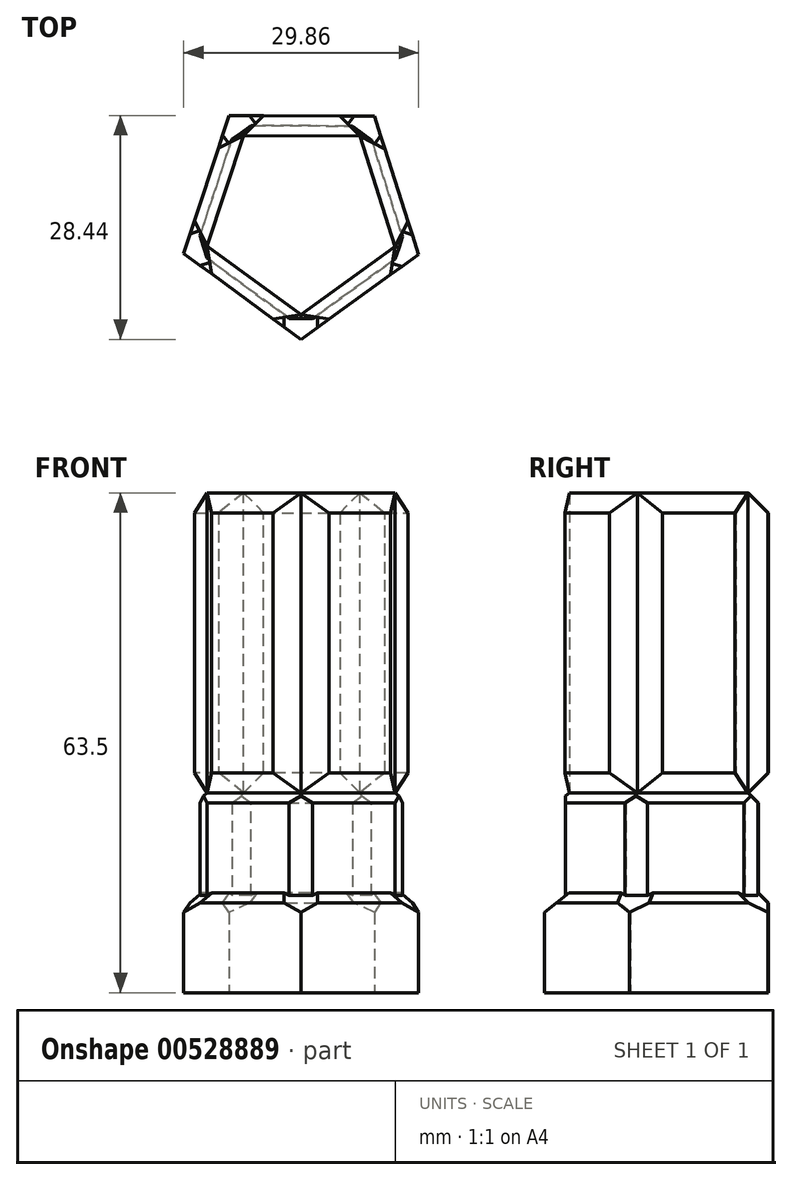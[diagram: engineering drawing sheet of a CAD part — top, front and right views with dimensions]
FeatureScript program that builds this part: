
annotation { "Feature Type Name" : "Feature", "Feature Type Description" : "" }
export const myFeature = defineFeature(function(context is Context, id is Id, definition is map)
    precondition{}
    {
        {
            var Q0;
            Q0=qCreatedBy(makeId("Top.planeOp"),FACE);
            var sketch = newSketch(context, id + "F0", { "sketchPlane" : qUnion([Q0])});
            skCircle(sketch, "E0.cCircle", {"center": v(-32.15, -43.23) * mm, "radius": 12.7 * mm, "construction": true});
            skLineSegment(sketch, "E0.0", {"start": v(-17.24, -48.15) * mm, "end": v(-32.22, -58.93) * mm});
            skLineSegment(sketch, "E0.1", {"start": v(-32.22, -58.93) * mm, "end": v(-47.1, -48.01) * mm});
            skLineSegment(sketch, "E0.2", {"start": v(-47.1, -48.01) * mm, "end": v(-41.32, -30.49) * mm});
            skLineSegment(sketch, "E0.3", {"start": v(-41.32, -30.49) * mm, "end": v(-22.86, -30.58) * mm});
            skLineSegment(sketch, "E0.4", {"start": v(-22.86, -30.58) * mm, "end": v(-17.24, -48.15) * mm});
            skPoint(sketch, "E0.0.midPoint", {"position": v(-24.73, -53.54) * mm});
            skSolve(sketch);
        }
        {
            var Q0;
            Q0=makeQuery(id+"F0.imprint","IMPRINT",FACE,{"disambiguationData":[TD([[makeQuery(id+"F0.imprint","IMPRINT",EDGE,{"derivedFrom":sQuery(id+"F0.wireOp",EDGE,"E0.0")}),-1.0]])]});
            extrude(context, id + "F1", {"entities" : qUnion([Q0]), "depth" : 12.7 * mm, "offsetDistance" : 25.4 * mm});
        }
        {
            var Q0;
            Q0=makeQuery(id+"F1.opExtrude","CAP_FACE",FACE,{"disambiguationData":[OSD([sQuery(id+"F0.wireOp",EDGE,"E0.0"),sQuery(id+"F0.wireOp",EDGE,"E0.1"),sQuery(id+"F0.wireOp",EDGE,"E0.2"),sQuery(id+"F0.wireOp",EDGE,"E0.3"),sQuery(id+"F0.wireOp",EDGE,"E0.4")])],"isStart":false});
            chamfer(context, id + "F2", {"entities" : qUnion([Q0]), "width" : 1.27 * mm, "tangentPropagation" : true});
        }
        {
            var Q0;
            Q0=makeQuery(id+"F1.opExtrude","CAP_FACE",FACE,{"disambiguationData":[OSD([sQuery(id+"F0.wireOp",EDGE,"E0.0"),sQuery(id+"F0.wireOp",EDGE,"E0.1"),sQuery(id+"F0.wireOp",EDGE,"E0.2"),sQuery(id+"F0.wireOp",EDGE,"E0.3"),sQuery(id+"F0.wireOp",EDGE,"E0.4")])],"isStart":false});
            extrude(context, id + "F3", {"entities" : qUnion([Q0]), "operationType" : NewBodyOperationType.ADD, "depth" : 12.7 * mm, "offsetDistance" : 25.4 * mm});
        }
        {
            var Q0;
            Q0=makeQuery(id+"F3.opExtrude","CAP_FACE",FACE,{"disambiguationData":[OSD([sQuery(id+"F0.wireOp",EDGE,"E0.0"),sQuery(id+"F0.wireOp",EDGE,"E0.1"),sQuery(id+"F0.wireOp",EDGE,"E0.2"),sQuery(id+"F0.wireOp",EDGE,"E0.3"),sQuery(id+"F0.wireOp",EDGE,"E0.4")])],"isStart":false});
            chamfer(context, id + "F4", {"entities" : qUnion([Q0]), "width" : 1.27 * mm, "tangentPropagation" : true});
        }
        {
            var Q0;
            Q0=makeQuery(id+"F3.opExtrude","CAP_FACE",FACE,{"disambiguationData":[OSD([sQuery(id+"F0.wireOp",EDGE,"E0.0"),sQuery(id+"F0.wireOp",EDGE,"E0.1"),sQuery(id+"F0.wireOp",EDGE,"E0.2"),sQuery(id+"F0.wireOp",EDGE,"E0.3"),sQuery(id+"F0.wireOp",EDGE,"E0.4")])],"isStart":false});
            extrude(context, id + "F5", {"entities" : qUnion([Q0]), "operationType" : NewBodyOperationType.ADD, "depth" : 38.1 * mm, "offsetDistance" : 25.4 * mm});
        }
        {
            var Q0;
            {var subQ0=sQuery(id+"F0.wireOp",EDGE,"E0.4");var subQ1=sQuery(id+"F0.wireOp",EDGE,"E0.3");var subQ2=sQuery(id+"F0.wireOp",EDGE,"E0.2");var subQ3=sQuery(id+"F0.wireOp",EDGE,"E0.1");var subQ4=sQuery(id+"F0.wireOp",EDGE,"E0.0");Q0=makeQuery(id+"F3.opExtrude","SWEPT_EDGE",EDGE,{"disambiguationData":[OSD([subQ4,subQ3,subQ2,subQ1,subQ0]),TDD([makeQuery(id+"F2.opChamfer","BLEND_VERTEX",VERTEX,{"blendedFrom":[makeQuery(id+"F1.opExtrude","CAP_EDGE",EDGE,{"disambiguationData":[OSD([subQ4])],"isStart":false}),makeQuery(id+"F1.opExtrude","CAP_EDGE",EDGE,{"disambiguationData":[OSD([subQ0])],"isStart":false}),makeQuery(id+"F1.opExtrude","CAP_FACE",FACE,{"disambiguationData":[OSD([subQ4,subQ3,subQ2,subQ1,subQ0])],"isStart":false})],"blendedInto":[makeQuery(id+"F1.opExtrude","CAP_FACE",FACE,{"disambiguationData":[OSD([subQ4,subQ3,subQ2,subQ1,subQ0])],"isStart":false})]})])]});}
            var Q1;
            {var subQ0=sQuery(id+"F0.wireOp",EDGE,"E0.4");var subQ1=sQuery(id+"F0.wireOp",EDGE,"E0.3");var subQ2=sQuery(id+"F0.wireOp",EDGE,"E0.2");var subQ3=sQuery(id+"F0.wireOp",EDGE,"E0.1");var subQ4=sQuery(id+"F0.wireOp",EDGE,"E0.0");Q1=makeQuery(id+"F3.opExtrude","SWEPT_EDGE",EDGE,{"disambiguationData":[OSD([subQ4,subQ3,subQ2,subQ1,subQ0]),TDD([makeQuery(id+"F2.opChamfer","BLEND_VERTEX",VERTEX,{"blendedFrom":[makeQuery(id+"F1.opExtrude","CAP_EDGE",EDGE,{"disambiguationData":[OSD([subQ4])],"isStart":false}),makeQuery(id+"F1.opExtrude","CAP_EDGE",EDGE,{"disambiguationData":[OSD([subQ3])],"isStart":false}),makeQuery(id+"F1.opExtrude","CAP_FACE",FACE,{"disambiguationData":[OSD([subQ4,subQ3,subQ2,subQ1,subQ0])],"isStart":false})],"blendedInto":[makeQuery(id+"F1.opExtrude","CAP_FACE",FACE,{"disambiguationData":[OSD([subQ4,subQ3,subQ2,subQ1,subQ0])],"isStart":false})]})])]});}
            var Q2;
            {var subQ0=sQuery(id+"F0.wireOp",EDGE,"E0.4");var subQ1=sQuery(id+"F0.wireOp",EDGE,"E0.3");var subQ2=sQuery(id+"F0.wireOp",EDGE,"E0.2");var subQ3=sQuery(id+"F0.wireOp",EDGE,"E0.1");var subQ4=sQuery(id+"F0.wireOp",EDGE,"E0.0");Q2=makeQuery(id+"F3.opExtrude","SWEPT_EDGE",EDGE,{"disambiguationData":[OSD([subQ4,subQ3,subQ2,subQ1,subQ0]),TDD([makeQuery(id+"F2.opChamfer","BLEND_VERTEX",VERTEX,{"blendedFrom":[makeQuery(id+"F1.opExtrude","CAP_EDGE",EDGE,{"disambiguationData":[OSD([subQ3])],"isStart":false}),makeQuery(id+"F1.opExtrude","CAP_EDGE",EDGE,{"disambiguationData":[OSD([subQ2])],"isStart":false}),makeQuery(id+"F1.opExtrude","CAP_FACE",FACE,{"disambiguationData":[OSD([subQ4,subQ3,subQ2,subQ1,subQ0])],"isStart":false})],"blendedInto":[makeQuery(id+"F1.opExtrude","CAP_FACE",FACE,{"disambiguationData":[OSD([subQ4,subQ3,subQ2,subQ1,subQ0])],"isStart":false})]})])]});}
            var Q3;
            {var subQ0=sQuery(id+"F0.wireOp",EDGE,"E0.4");var subQ1=sQuery(id+"F0.wireOp",EDGE,"E0.3");var subQ2=sQuery(id+"F0.wireOp",EDGE,"E0.2");var subQ3=sQuery(id+"F0.wireOp",EDGE,"E0.1");var subQ4=sQuery(id+"F0.wireOp",EDGE,"E0.0");Q3=makeQuery(id+"F3.opExtrude","SWEPT_EDGE",EDGE,{"disambiguationData":[OSD([subQ4,subQ3,subQ2,subQ1,subQ0]),TDD([makeQuery(id+"F2.opChamfer","BLEND_VERTEX",VERTEX,{"blendedFrom":[makeQuery(id+"F1.opExtrude","CAP_EDGE",EDGE,{"disambiguationData":[OSD([subQ2])],"isStart":false}),makeQuery(id+"F1.opExtrude","CAP_EDGE",EDGE,{"disambiguationData":[OSD([subQ1])],"isStart":false}),makeQuery(id+"F1.opExtrude","CAP_FACE",FACE,{"disambiguationData":[OSD([subQ4,subQ3,subQ2,subQ1,subQ0])],"isStart":false})],"blendedInto":[makeQuery(id+"F1.opExtrude","CAP_FACE",FACE,{"disambiguationData":[OSD([subQ4,subQ3,subQ2,subQ1,subQ0])],"isStart":false})]})])]});}
            var Q4;
            {var subQ0=sQuery(id+"F0.wireOp",EDGE,"E0.4");var subQ1=sQuery(id+"F0.wireOp",EDGE,"E0.3");var subQ2=sQuery(id+"F0.wireOp",EDGE,"E0.2");var subQ3=sQuery(id+"F0.wireOp",EDGE,"E0.1");var subQ4=sQuery(id+"F0.wireOp",EDGE,"E0.0");Q4=makeQuery(id+"F3.opExtrude","SWEPT_EDGE",EDGE,{"disambiguationData":[OSD([subQ4,subQ3,subQ2,subQ1,subQ0]),TDD([makeQuery(id+"F2.opChamfer","BLEND_VERTEX",VERTEX,{"blendedFrom":[makeQuery(id+"F1.opExtrude","CAP_EDGE",EDGE,{"disambiguationData":[OSD([subQ1])],"isStart":false}),makeQuery(id+"F1.opExtrude","CAP_EDGE",EDGE,{"disambiguationData":[OSD([subQ0])],"isStart":false}),makeQuery(id+"F1.opExtrude","CAP_FACE",FACE,{"disambiguationData":[OSD([subQ4,subQ3,subQ2,subQ1,subQ0])],"isStart":false})],"blendedInto":[makeQuery(id+"F1.opExtrude","CAP_FACE",FACE,{"disambiguationData":[OSD([subQ4,subQ3,subQ2,subQ1,subQ0])],"isStart":false})]})])]});}
            chamfer(context, id + "F6", {"entities" : qUnion([Q0, Q1, Q2, Q3, Q4]), "width" : 2.54 * mm, "tangentPropagation" : true});
        }
        {
            var Q0;
            {var subQ0=sQuery(id+"F0.wireOp",EDGE,"E0.4");var subQ1=sQuery(id+"F0.wireOp",EDGE,"E0.3");var subQ2=sQuery(id+"F0.wireOp",EDGE,"E0.2");var subQ3=sQuery(id+"F0.wireOp",EDGE,"E0.1");var subQ4=sQuery(id+"F0.wireOp",EDGE,"E0.0");Q0=makeQuery(id+"F5.opExtrude","SWEPT_FACE",FACE,{"disambiguationData":[OSD([subQ4,subQ3,subQ2,subQ1,subQ0]),TDD([makeQuery(id+"F4.opChamfer","BLEND_EDGE",EDGE,{"blendedFrom":[makeQuery(id+"F3.opExtrude","CAP_EDGE",EDGE,{"disambiguationData":[OSD([subQ4,subQ3,subQ2,subQ1,subQ0]),TDD([makeQuery(id+"F2.opChamfer","BLEND_EDGE",EDGE,{"blendedFrom":[makeQuery(id+"F1.opExtrude","CAP_EDGE",EDGE,{"disambiguationData":[OSD([subQ1])],"isStart":false}),makeQuery(id+"F1.opExtrude","CAP_FACE",FACE,{"disambiguationData":[OSD([subQ4,subQ3,subQ2,subQ1,subQ0])],"isStart":false})],"blendedInto":[makeQuery(id+"F1.opExtrude","CAP_FACE",FACE,{"disambiguationData":[OSD([subQ4,subQ3,subQ2,subQ1,subQ0])],"isStart":false})]})])],"isStart":false}),makeQuery(id+"F3.opExtrude","CAP_FACE",FACE,{"disambiguationData":[OSD([subQ4,subQ3,subQ2,subQ1,subQ0])],"isStart":false})],"blendedInto":[makeQuery(id+"F3.opExtrude","CAP_FACE",FACE,{"disambiguationData":[OSD([subQ4,subQ3,subQ2,subQ1,subQ0])],"isStart":false})]})])]});}
            extrude(context, id + "F7", {"entities" : qUnion([Q0]), "operationType" : NewBodyOperationType.ADD, "depth" : 2.54 * mm, "offsetDistance" : 25.4 * mm});
        }
        {
            var Q0;
            {var subQ0=sQuery(id+"F0.wireOp",EDGE,"E0.4");var subQ1=sQuery(id+"F0.wireOp",EDGE,"E0.3");var subQ2=sQuery(id+"F0.wireOp",EDGE,"E0.2");var subQ3=sQuery(id+"F0.wireOp",EDGE,"E0.1");var subQ4=sQuery(id+"F0.wireOp",EDGE,"E0.0");Q0=makeQuery(id+"F5.opExtrude","SWEPT_FACE",FACE,{"disambiguationData":[OSD([subQ4,subQ3,subQ2,subQ1,subQ0]),TDD([makeQuery(id+"F4.opChamfer","BLEND_EDGE",EDGE,{"blendedFrom":[makeQuery(id+"F3.opExtrude","CAP_EDGE",EDGE,{"disambiguationData":[OSD([subQ4,subQ3,subQ2,subQ1,subQ0]),TDD([makeQuery(id+"F2.opChamfer","BLEND_EDGE",EDGE,{"blendedFrom":[makeQuery(id+"F1.opExtrude","CAP_EDGE",EDGE,{"disambiguationData":[OSD([subQ2])],"isStart":false}),makeQuery(id+"F1.opExtrude","CAP_FACE",FACE,{"disambiguationData":[OSD([subQ4,subQ3,subQ2,subQ1,subQ0])],"isStart":false})],"blendedInto":[makeQuery(id+"F1.opExtrude","CAP_FACE",FACE,{"disambiguationData":[OSD([subQ4,subQ3,subQ2,subQ1,subQ0])],"isStart":false})]})])],"isStart":false}),makeQuery(id+"F3.opExtrude","CAP_FACE",FACE,{"disambiguationData":[OSD([subQ4,subQ3,subQ2,subQ1,subQ0])],"isStart":false})],"blendedInto":[makeQuery(id+"F3.opExtrude","CAP_FACE",FACE,{"disambiguationData":[OSD([subQ4,subQ3,subQ2,subQ1,subQ0])],"isStart":false})]})])]});}
            extrude(context, id + "F8", {"entities" : qUnion([Q0]), "operationType" : NewBodyOperationType.ADD, "depth" : 2.54 * mm, "offsetDistance" : 25.4 * mm});
        }
        {
            var Q0;
            {var subQ0=sQuery(id+"F0.wireOp",EDGE,"E0.4");var subQ1=sQuery(id+"F0.wireOp",EDGE,"E0.3");var subQ2=sQuery(id+"F0.wireOp",EDGE,"E0.2");var subQ3=sQuery(id+"F0.wireOp",EDGE,"E0.1");var subQ4=sQuery(id+"F0.wireOp",EDGE,"E0.0");Q0=makeQuery(id+"F5.opExtrude","SWEPT_FACE",FACE,{"disambiguationData":[OSD([subQ4,subQ3,subQ2,subQ1,subQ0]),TDD([makeQuery(id+"F4.opChamfer","BLEND_EDGE",EDGE,{"blendedFrom":[makeQuery(id+"F3.opExtrude","CAP_EDGE",EDGE,{"disambiguationData":[OSD([subQ4,subQ3,subQ2,subQ1,subQ0]),TDD([makeQuery(id+"F2.opChamfer","BLEND_EDGE",EDGE,{"blendedFrom":[makeQuery(id+"F1.opExtrude","CAP_EDGE",EDGE,{"disambiguationData":[OSD([subQ3])],"isStart":false}),makeQuery(id+"F1.opExtrude","CAP_FACE",FACE,{"disambiguationData":[OSD([subQ4,subQ3,subQ2,subQ1,subQ0])],"isStart":false})],"blendedInto":[makeQuery(id+"F1.opExtrude","CAP_FACE",FACE,{"disambiguationData":[OSD([subQ4,subQ3,subQ2,subQ1,subQ0])],"isStart":false})]})])],"isStart":false}),makeQuery(id+"F3.opExtrude","CAP_FACE",FACE,{"disambiguationData":[OSD([subQ4,subQ3,subQ2,subQ1,subQ0])],"isStart":false})],"blendedInto":[makeQuery(id+"F3.opExtrude","CAP_FACE",FACE,{"disambiguationData":[OSD([subQ4,subQ3,subQ2,subQ1,subQ0])],"isStart":false})]})])]});}
            extrude(context, id + "F9", {"entities" : qUnion([Q0]), "operationType" : NewBodyOperationType.ADD, "depth" : 2.54 * mm, "offsetDistance" : 25.4 * mm});
        }
        {
            var Q0;
            {var subQ0=sQuery(id+"F0.wireOp",EDGE,"E0.4");var subQ1=sQuery(id+"F0.wireOp",EDGE,"E0.3");var subQ2=sQuery(id+"F0.wireOp",EDGE,"E0.2");var subQ3=sQuery(id+"F0.wireOp",EDGE,"E0.1");var subQ4=sQuery(id+"F0.wireOp",EDGE,"E0.0");Q0=makeQuery(id+"F5.opExtrude","SWEPT_FACE",FACE,{"disambiguationData":[OSD([subQ4,subQ3,subQ2,subQ1,subQ0]),TDD([makeQuery(id+"F4.opChamfer","BLEND_EDGE",EDGE,{"blendedFrom":[makeQuery(id+"F3.opExtrude","CAP_EDGE",EDGE,{"disambiguationData":[OSD([subQ4,subQ3,subQ2,subQ1,subQ0]),TDD([makeQuery(id+"F2.opChamfer","BLEND_EDGE",EDGE,{"blendedFrom":[makeQuery(id+"F1.opExtrude","CAP_EDGE",EDGE,{"disambiguationData":[OSD([subQ4])],"isStart":false}),makeQuery(id+"F1.opExtrude","CAP_FACE",FACE,{"disambiguationData":[OSD([subQ4,subQ3,subQ2,subQ1,subQ0])],"isStart":false})],"blendedInto":[makeQuery(id+"F1.opExtrude","CAP_FACE",FACE,{"disambiguationData":[OSD([subQ4,subQ3,subQ2,subQ1,subQ0])],"isStart":false})]})])],"isStart":false}),makeQuery(id+"F3.opExtrude","CAP_FACE",FACE,{"disambiguationData":[OSD([subQ4,subQ3,subQ2,subQ1,subQ0])],"isStart":false})],"blendedInto":[makeQuery(id+"F3.opExtrude","CAP_FACE",FACE,{"disambiguationData":[OSD([subQ4,subQ3,subQ2,subQ1,subQ0])],"isStart":false})]})])]});}
            extrude(context, id + "F10", {"entities" : qUnion([Q0]), "operationType" : NewBodyOperationType.ADD, "depth" : 2.54 * mm, "offsetDistance" : 25.4 * mm});
        }
        {
            var Q0;
            {var subQ0=sQuery(id+"F0.wireOp",EDGE,"E0.4");var subQ1=sQuery(id+"F0.wireOp",EDGE,"E0.3");var subQ2=sQuery(id+"F0.wireOp",EDGE,"E0.2");var subQ3=sQuery(id+"F0.wireOp",EDGE,"E0.1");var subQ4=sQuery(id+"F0.wireOp",EDGE,"E0.0");Q0=makeQuery(id+"F5.opExtrude","SWEPT_FACE",FACE,{"disambiguationData":[OSD([subQ4,subQ3,subQ2,subQ1,subQ0]),TDD([makeQuery(id+"F4.opChamfer","BLEND_EDGE",EDGE,{"blendedFrom":[makeQuery(id+"F3.opExtrude","CAP_EDGE",EDGE,{"disambiguationData":[OSD([subQ4,subQ3,subQ2,subQ1,subQ0]),TDD([makeQuery(id+"F2.opChamfer","BLEND_EDGE",EDGE,{"blendedFrom":[makeQuery(id+"F1.opExtrude","CAP_EDGE",EDGE,{"disambiguationData":[OSD([subQ0])],"isStart":false}),makeQuery(id+"F1.opExtrude","CAP_FACE",FACE,{"disambiguationData":[OSD([subQ4,subQ3,subQ2,subQ1,subQ0])],"isStart":false})],"blendedInto":[makeQuery(id+"F1.opExtrude","CAP_FACE",FACE,{"disambiguationData":[OSD([subQ4,subQ3,subQ2,subQ1,subQ0])],"isStart":false})]})])],"isStart":false}),makeQuery(id+"F3.opExtrude","CAP_FACE",FACE,{"disambiguationData":[OSD([subQ4,subQ3,subQ2,subQ1,subQ0])],"isStart":false})],"blendedInto":[makeQuery(id+"F3.opExtrude","CAP_FACE",FACE,{"disambiguationData":[OSD([subQ4,subQ3,subQ2,subQ1,subQ0])],"isStart":false})]})])]});}
            extrude(context, id + "F11", {"entities" : qUnion([Q0]), "operationType" : NewBodyOperationType.ADD, "depth" : 2.54 * mm, "offsetDistance" : 25.4 * mm});
        }
        {
            var Q0;
            Q0=makeQuery(id+"F10.opExtrude","CAP_FACE",FACE,{"disambiguationData":[OSD([sQuery(id+"F0.wireOp",EDGE,"E0.0"),sQuery(id+"F0.wireOp",EDGE,"E0.1"),sQuery(id+"F0.wireOp",EDGE,"E0.2"),sQuery(id+"F0.wireOp",EDGE,"E0.3"),sQuery(id+"F0.wireOp",EDGE,"E0.4")])],"isStart":false});
            chamfer(context, id + "F12", {"entities" : qUnion([Q0]), "width" : 2.54 * mm, "tangentPropagation" : true});
        }
        {
            var Q0;
            Q0=makeQuery(id+"F11.opExtrude","CAP_FACE",FACE,{"disambiguationData":[OSD([sQuery(id+"F0.wireOp",EDGE,"E0.0"),sQuery(id+"F0.wireOp",EDGE,"E0.1"),sQuery(id+"F0.wireOp",EDGE,"E0.2"),sQuery(id+"F0.wireOp",EDGE,"E0.3"),sQuery(id+"F0.wireOp",EDGE,"E0.4")])],"isStart":false});
            var Q1;
            Q1=makeQuery(id+"F7.opExtrude","CAP_FACE",FACE,{"disambiguationData":[OSD([sQuery(id+"F0.wireOp",EDGE,"E0.0"),sQuery(id+"F0.wireOp",EDGE,"E0.1"),sQuery(id+"F0.wireOp",EDGE,"E0.2"),sQuery(id+"F0.wireOp",EDGE,"E0.3"),sQuery(id+"F0.wireOp",EDGE,"E0.4")])],"isStart":false});
            var Q2;
            Q2=makeQuery(id+"F8.opExtrude","CAP_FACE",FACE,{"disambiguationData":[OSD([sQuery(id+"F0.wireOp",EDGE,"E0.0"),sQuery(id+"F0.wireOp",EDGE,"E0.1"),sQuery(id+"F0.wireOp",EDGE,"E0.2"),sQuery(id+"F0.wireOp",EDGE,"E0.3"),sQuery(id+"F0.wireOp",EDGE,"E0.4")])],"isStart":false});
            var Q3;
            Q3=makeQuery(id+"F9.opExtrude","CAP_FACE",FACE,{"disambiguationData":[OSD([sQuery(id+"F0.wireOp",EDGE,"E0.0"),sQuery(id+"F0.wireOp",EDGE,"E0.1"),sQuery(id+"F0.wireOp",EDGE,"E0.2"),sQuery(id+"F0.wireOp",EDGE,"E0.3"),sQuery(id+"F0.wireOp",EDGE,"E0.4")])],"isStart":false});
            chamfer(context, id + "F13", {"entities" : qUnion([Q0, Q1, Q2, Q3]), "width" : 2.54 * mm, "tangentPropagation" : true});
        }
        {
            var Q0;
            Q0=makeQuery(id+"F2.opChamfer","BLEND_EDGE",EDGE,{"blendedFrom":[makeQuery(id+"F1.opExtrude","CAP_EDGE",EDGE,{"disambiguationData":[OSD([sQuery(id+"F0.wireOp",EDGE,"E0.0")])],"isStart":false}),makeQuery(id+"F1.opExtrude","CAP_EDGE",EDGE,{"disambiguationData":[OSD([sQuery(id+"F0.wireOp",EDGE,"E0.1")])],"isStart":false})],"blendedInto":[]});
            var Q1;
            Q1=makeQuery(id+"F2.opChamfer","BLEND_EDGE",EDGE,{"blendedFrom":[makeQuery(id+"F1.opExtrude","CAP_EDGE",EDGE,{"disambiguationData":[OSD([sQuery(id+"F0.wireOp",EDGE,"E0.0")])],"isStart":false}),makeQuery(id+"F1.opExtrude","CAP_EDGE",EDGE,{"disambiguationData":[OSD([sQuery(id+"F0.wireOp",EDGE,"E0.4")])],"isStart":false})],"blendedInto":[]});
            var Q2;
            Q2=makeQuery(id+"F2.opChamfer","BLEND_EDGE",EDGE,{"blendedFrom":[makeQuery(id+"F1.opExtrude","CAP_EDGE",EDGE,{"disambiguationData":[OSD([sQuery(id+"F0.wireOp",EDGE,"E0.3")])],"isStart":false}),makeQuery(id+"F1.opExtrude","CAP_EDGE",EDGE,{"disambiguationData":[OSD([sQuery(id+"F0.wireOp",EDGE,"E0.4")])],"isStart":false})],"blendedInto":[]});
            var Q3;
            Q3=makeQuery(id+"F2.opChamfer","BLEND_EDGE",EDGE,{"blendedFrom":[makeQuery(id+"F1.opExtrude","CAP_EDGE",EDGE,{"disambiguationData":[OSD([sQuery(id+"F0.wireOp",EDGE,"E0.2")])],"isStart":false}),makeQuery(id+"F1.opExtrude","CAP_EDGE",EDGE,{"disambiguationData":[OSD([sQuery(id+"F0.wireOp",EDGE,"E0.3")])],"isStart":false})],"blendedInto":[]});
            var Q4;
            Q4=makeQuery(id+"F2.opChamfer","BLEND_EDGE",EDGE,{"blendedFrom":[makeQuery(id+"F1.opExtrude","CAP_EDGE",EDGE,{"disambiguationData":[OSD([sQuery(id+"F0.wireOp",EDGE,"E0.1")])],"isStart":false}),makeQuery(id+"F1.opExtrude","CAP_EDGE",EDGE,{"disambiguationData":[OSD([sQuery(id+"F0.wireOp",EDGE,"E0.2")])],"isStart":false})],"blendedInto":[]});
            chamfer(context, id + "F14", {"entities" : qUnion([Q0, Q1, Q2, Q3, Q4]), "width" : 5.08 * mm, "tangentPropagation" : true});
        }
    });
